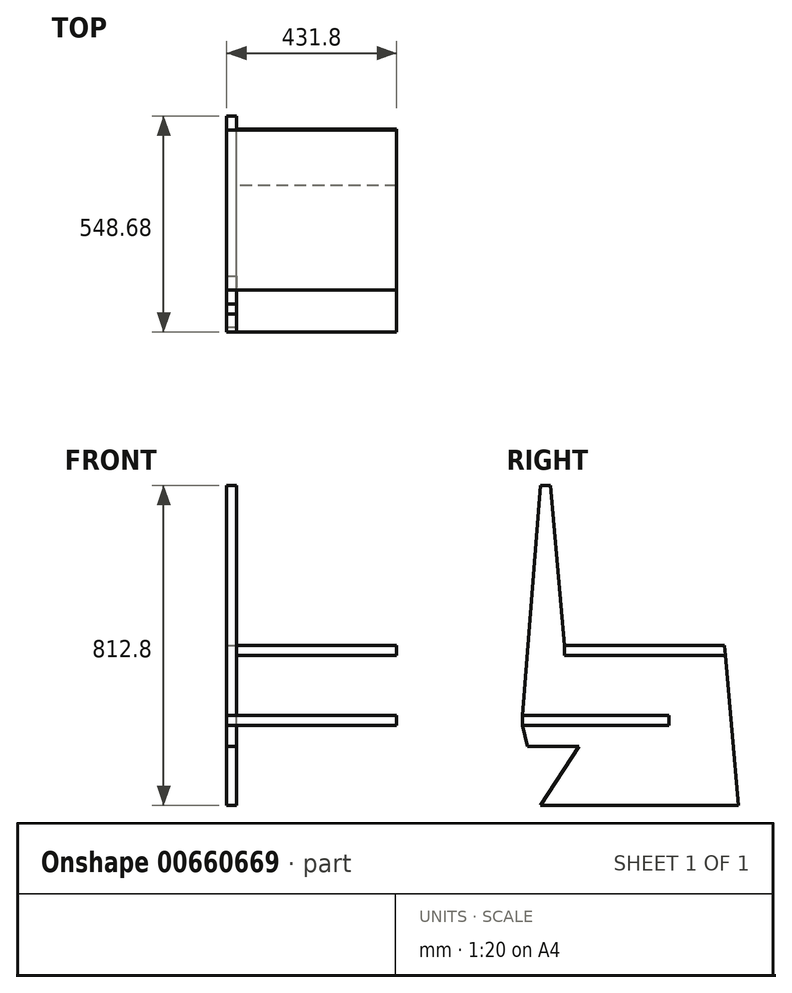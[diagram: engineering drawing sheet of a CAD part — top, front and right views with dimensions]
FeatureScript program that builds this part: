
annotation { "Feature Type Name" : "Feature", "Feature Type Description" : "" }
export const myFeature = defineFeature(function(context is Context, id is Id, definition is map)
    precondition{}
    {
        {
            var Q0;
            Q0=qCreatedBy(makeId("Right.planeOp"),FACE);
            var sketch = newSketch(context, id + "F0", { "sketchPlane" : qUnion([Q0])});
            skLineSegment(sketch, "E0", {"start": v(0, 0) * mm, "end": v(0, 203.2) * mm});
            skLineSegment(sketch, "E1", {"start": v(203.2, 203.2) * mm, "end": v(0, 203.2) * mm});
            skLineSegment(sketch, "E2", {"start": v(203.2, 203.2) * mm, "end": v(203.2, 406.4) * mm});
            skLineSegment(sketch, "E3", {"start": v(203.2, 406.4) * mm, "end": v(406.4, 406.4) * mm});
            skLineSegment(sketch, "E4", {"start": v(406.4, 406.4) * mm, "end": v(406.4, 609.6) * mm});
            skLineSegment(sketch, "E5", {"start": v(406.4, 609.6) * mm, "end": v(609.6, 609.6) * mm});
            skLineSegment(sketch, "E6", {"start": v(609.6, 0) * mm, "end": v(0, 0) * mm});
            skLineSegment(sketch, "E7", {"start": v(-283.6, 0) * mm, "end": v(-319.16, 406.4) * mm});
            skLineSegment(sketch, "E8", {"start": v(609.6, 609.6) * mm, "end": v(609.6, 0) * mm});
            skLineSegment(sketch, "E9", {"start": v(-319.16, 406.4) * mm, "end": v(-725.56, 406.4) * mm});
            skLineSegment(sketch, "E10", {"start": v(-725.56, 406.4) * mm, "end": v(-725.56, 812.8) * mm, "construction": true});
            skLineSegment(sketch, "E11", {"start": v(-761.31, 815.01) * mm, "end": v(-725.56, 406.4) * mm});
            skLineSegment(sketch, "E12", {"start": v(-761.31, 815.01) * mm, "end": v(-786.62, 812.8) * mm});
            skLineSegment(sketch, "E13", {"start": v(-786.62, 812.8) * mm, "end": v(-748.84, 381) * mm});
            skLineSegment(sketch, "E14", {"start": v(-748.84, 381) * mm, "end": v(-316.94, 381) * mm});
            skLineSegment(sketch, "E15", {"start": v(-786.62, 0) * mm, "end": v(-538.88, 381) * mm});
            skLineSegment(sketch, "E16", {"start": v(-522.36, 406.4) * mm, "end": v(-538.88, 381) * mm});
            skLineSegment(sketch, "E17", {"start": v(203.2, 406.4) * mm, "end": v(-969.43, 406.4) * mm, "construction": true});
            skLineSegment(sketch, "E18", {"start": v(406.4, 406.4) * mm, "end": v(406.4, 0) * mm});
            skLineSegment(sketch, "E19", {"start": v(-761.12, 812.8) * mm, "end": v(-725.56, 812.8) * mm});
            skLineSegment(sketch, "E20", {"start": v(-786.62, 0) * mm, "end": v(-319.16, 0) * mm});
            skLineSegment(sketch, "E21", {"start": v(-319.16, 0) * mm, "end": v(-283.6, 0) * mm});
            skLineSegment(sketch, "E22", {"start": v(-319.16, 0) * mm, "end": v(-319.16, 406.4) * mm, "construction": true});
            skLineSegment(sketch, "E23", {"start": v(-761.12, 812.8) * mm, "end": v(-786.62, 812.8) * mm});
            skLineSegment(sketch, "E24", {"start": v(0, 203.2) * mm, "end": v(-969.43, 203.2) * mm, "construction": true});
            skLineSegment(sketch, "E25", {"start": v(-654.49, 203.2) * mm, "end": v(-460.17, 203.2) * mm});
            skLineSegment(sketch, "E26", {"start": v(-460.17, 203.2) * mm, "end": v(-460.17, 228.6) * mm});
            skLineSegment(sketch, "E27", {"start": v(-460.17, 228.6) * mm, "end": v(-637.97, 228.6) * mm});
            skLineSegment(sketch, "E28", {"start": v(-654.49, 203.2) * mm, "end": v(-832.29, 203.2) * mm});
            skLineSegment(sketch, "E29", {"start": v(-832.29, 203.2) * mm, "end": v(-832.29, 228.6) * mm});
            skLineSegment(sketch, "E30", {"start": v(-832.29, 228.6) * mm, "end": v(-637.97, 228.6) * mm});
            skLineSegment(sketch, "E31", {"start": v(-786.62, 0) * mm, "end": v(-786.62, 812.8) * mm, "construction": true});
            skLineSegment(sketch, "E32", {"start": v(-832.29, 203.2) * mm, "end": v(-786.62, 0) * mm});
            skLineSegment(sketch, "E33", {"start": v(-786.62, 812.8) * mm, "end": v(-832.29, 228.6) * mm});
            skLineSegment(sketch, "E34", {"start": v(-725.56, 406.4) * mm, "end": v(-725.56, 381) * mm});
            skLineSegment(sketch, "E35", {"start": v(-689.43, 149.47) * mm, "end": v(-820.21, 149.47) * mm});
            skSolve(sketch);
        }
        {
            var Q0;
            {var subQ0=sQuery(id+"F0.wireOp",EDGE,"E30");Q0=makeQuery(id+"F0.imprint","IMPRINT",FACE,{"disambiguationData":[TD([[makeQuery(id+"F0.imprint","IMPRINT",EDGE,{"derivedFrom":subQ0}),1.0]])]});}
            var Q1;
            {var subQ8=sQuery(id+"F0.wireOp",EDGE,"E16");Q1=makeQuery(id+"F0.imprint","IMPRINT",FACE,{"disambiguationData":[TD([[makeQuery(id+"F0.imprint","IMPRINT",EDGE,{"derivedFrom":subQ8}),-1.0]])]});}
            var Q2;
            {var subQ0=sQuery(id+"F0.wireOp",EDGE,"E28");Q2=makeQuery(id+"F0.imprint","IMPRINT",FACE,{"disambiguationData":[TD([[makeQuery(id+"F0.imprint","IMPRINT",EDGE,{"derivedFrom":subQ0}),1.0]])]});}
            var Q3;
            {var subQ0=sQuery(id+"F0.wireOp",EDGE,"E28");Q3=makeQuery(id+"F0.imprint","IMPRINT",FACE,{"disambiguationData":[TD([[makeQuery(id+"F0.imprint","IMPRINT",EDGE,{"derivedFrom":subQ0}),-1.0]])]});}
            var Q4;
            {var subQ4=sQuery(id+"F0.wireOp",EDGE,"E23");Q4=makeQuery(id+"F0.imprint","IMPRINT",FACE,{"disambiguationData":[TD([[makeQuery(id+"F0.imprint","IMPRINT",EDGE,{"derivedFrom":subQ4}),1.0]])]});}
            extrude(context, id + "F1", {"entities" : qUnion([Q0, Q1, Q2, Q3, Q4]), "oppositeDirection" : true, "depth" : 25.4 * mm, "offsetDistance" : 25.4 * mm});
        }
        {
            var Q0;
            {var subQ0=sQuery(id+"F0.wireOp",EDGE,"E20");Q0=makeQuery(id+"F0.imprint","IMPRINT",FACE,{"disambiguationData":[TD([[makeQuery(id+"F0.imprint","IMPRINT",EDGE,{"derivedFrom":subQ0}),1.0]])]});}
            var Q1;
            {var subQ0=sQuery(id+"F0.wireOp",EDGE,"E21");Q1=makeQuery(id+"F0.imprint","IMPRINT",FACE,{"disambiguationData":[TD([[makeQuery(id+"F0.imprint","IMPRINT",EDGE,{"derivedFrom":subQ0}),1.0]])]});}
            var Q2;
            {var subQ0=sQuery(id+"F0.wireOp",EDGE,"E16");Q2=makeQuery(id+"F0.imprint","IMPRINT",FACE,{"disambiguationData":[TD([[makeQuery(id+"F0.imprint","IMPRINT",EDGE,{"derivedFrom":subQ0}),1.0]])]});}
            var Q3;
            {var subQ1=sQuery(id+"F0.wireOp",EDGE,"E7");var subQ3=sQuery(id+"F0.wireOp",EDGE,"E14");var subQ4=makeQuery(id+"F0.imprint","INTERSECT",VERTEX,{"derivedFrom":[subQ1,subQ3]});Q3=makeQuery(id+"F0.imprint","IMPRINT",FACE,{"disambiguationData":[TD([[makeQuery(id+"F0.imprint","IMPRINT",EDGE,{"disambiguationData":[TD([[subQ4,1.0]])],"derivedFrom":subQ3}),1.0]])]});}
            var Q4;
            {var subQ0=sQuery(id+"F0.wireOp",EDGE,"E25");Q4=makeQuery(id+"F0.imprint","IMPRINT",FACE,{"disambiguationData":[TD([[makeQuery(id+"F0.imprint","IMPRINT",EDGE,{"derivedFrom":subQ0}),1.0]])]});}
            extrude(context, id + "F2", {"entities" : qUnion([Q0, Q1, Q2, Q3, Q4]), "oppositeDirection" : true, "depth" : 25.4 * mm, "offsetDistance" : 25.4 * mm});
        }
        {
            var Q0;
            {var subQ0=sQuery(id+"F0.wireOp",EDGE,"E28");Q0=makeQuery(id+"F0.imprint","IMPRINT",FACE,{"disambiguationData":[TD([[makeQuery(id+"F0.imprint","IMPRINT",EDGE,{"derivedFrom":subQ0}),-1.0]])]});}
            var Q1;
            {var subQ2=sQuery(id+"F0.wireOp",EDGE,"E16");Q1=makeQuery(id+"F0.imprint","IMPRINT",FACE,{"disambiguationData":[TD([[makeQuery(id+"F0.imprint","IMPRINT",EDGE,{"derivedFrom":subQ2}),-1.0]])]});}
            extrude(context, id + "F3", {"entities" : qUnion([Q0, Q1]), "operationType" : NewBodyOperationType.ADD, "depth" : 406.4 * mm, "offsetDistance" : 25.4 * mm});
        }
        {
            var Q0;
            {var subQ0=sQuery(id+"F0.wireOp",EDGE,"E25");Q0=makeQuery(id+"F0.imprint","IMPRINT",FACE,{"disambiguationData":[TD([[makeQuery(id+"F0.imprint","IMPRINT",EDGE,{"derivedFrom":subQ0}),1.0]])]});}
            var Q1;
            {var subQ5=sQuery(id+"F0.wireOp",EDGE,"E16");Q1=makeQuery(id+"F0.imprint","IMPRINT",FACE,{"disambiguationData":[TD([[makeQuery(id+"F0.imprint","IMPRINT",EDGE,{"derivedFrom":subQ5}),1.0]])]});}
            extrude(context, id + "F4", {"entities" : qUnion([Q0, Q1]), "operationType" : NewBodyOperationType.ADD, "depth" : 406.4 * mm, "offsetDistance" : 25.4 * mm});
        }
    });
